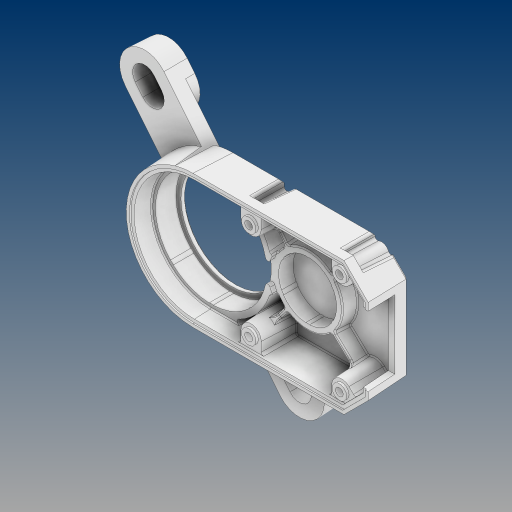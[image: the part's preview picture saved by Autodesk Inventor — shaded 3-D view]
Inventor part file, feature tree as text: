
AUTODESK INVENTOR PART (.ipt)
format: ipt  version: 2024.3 (Build 283343000, 343)  size: 991,744 bytes
history: native  units: in
note: dims shown in document units (in); Inventor stores cm internally (conversion verified against a paired STEP export)
features: fillet x1
ambient origin geometry x8: Origin, YZ Plane, XZ Plane, XY Plane, X Axis, Y Axis, Z Axis, Center Point
bodies: Solid1 (feature_tree)
feature tree (1):
  fillet  "Fillet11"  [1 undecoded]
note: 1 required parameter value undecoded (feature->parameter linkage not recoverable at this tier; creation-order binding heuristic only, values carry confidence <= 0.55)
